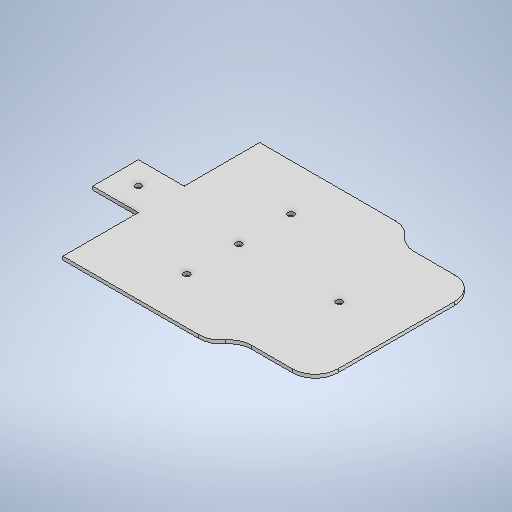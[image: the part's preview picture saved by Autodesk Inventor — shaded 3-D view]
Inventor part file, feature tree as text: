
AUTODESK INVENTOR PART (.ipt)
format: ipt  version: 2025.2 (Build 292293000, 293)  size: 265,728 bytes
history: native  units: mm
features: extrude x1, fillet x1, sketch x1
ambient origin geometry x8: Origin, YZ Plane, XZ Plane, XY Plane, X Axis, Y Axis, Z Axis, Center Point
bodies: Solid1 (feature_tree)
feature tree (3):
  extrude  "Extrusion1"  Depth=40.0mm
  fillet  "Fillet6"  Radius=3.0mm
  sketch  "Sketch1"  dims[d0=40.0mm d1=40.0mm d5=3.0mm d6=0.0mm d7=5.5mm d24=75.0mm d25=15.0mm d26=75.0mm d27=15.0mm d28=20.0mm d29=5.5mm d30=5.5mm d31=5.5mm d32=5.5mm d21=0.0mm d22=0.0mm d23=0.0mm]
